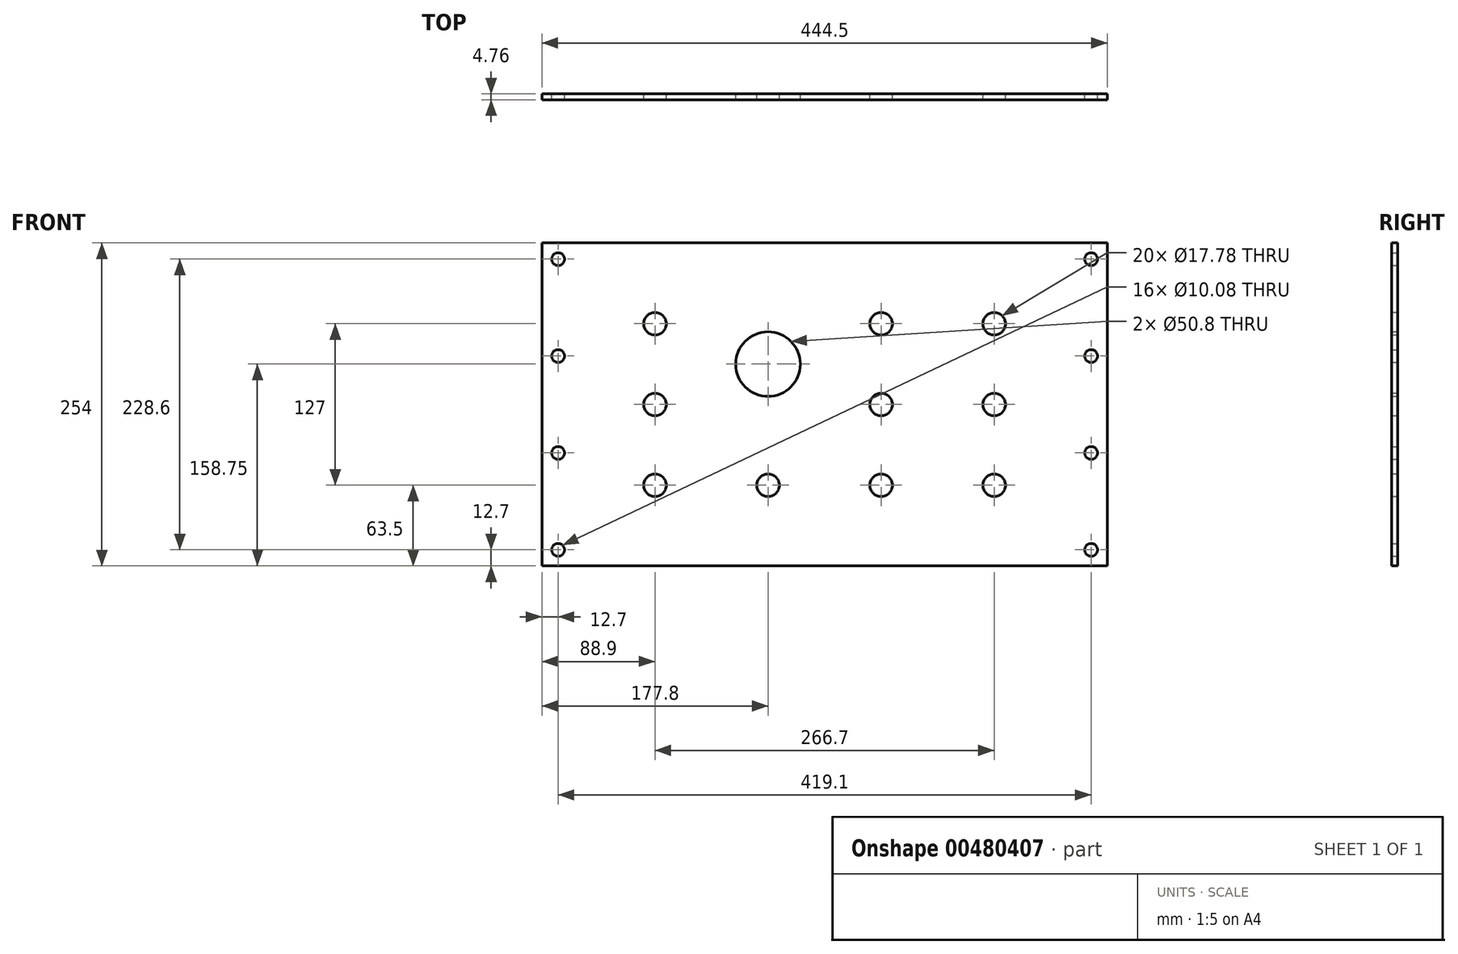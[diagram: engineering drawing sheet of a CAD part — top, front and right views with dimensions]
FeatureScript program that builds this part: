
annotation { "Feature Type Name" : "Feature", "Feature Type Description" : "" }
export const myFeature = defineFeature(function(context is Context, id is Id, definition is map)
    precondition{}
    {
        {
            var Q0;
            Q0=qCreatedBy(makeId("Front.planeOp"),FACE);
            var sketch = newSketch(context, id + "F0", { "sketchPlane" : qUnion([Q0])});
            skLineSegment(sketch, "E0.bottom", {"start": v(-222.25, 127) * mm, "end": v(222.25, 127) * mm});
            skLineSegment(sketch, "E0.top", {"start": v(-222.25, -127) * mm, "end": v(222.25, -127) * mm});
            skLineSegment(sketch, "E0.left", {"start": v(-222.25, 127) * mm, "end": v(-222.25, -127) * mm});
            skLineSegment(sketch, "E0.right", {"start": v(222.25, 127) * mm, "end": v(222.25, -127) * mm});
            skPoint(sketch, "E0.middle", {"position": v(0, 0) * mm});
            skCircle(sketch, "E1", {"center": v(-44.45, 31.75) * mm, "radius": 25.4 * mm});
            skCircle(sketch, "E2", {"center": v(209.55, 114.3) * mm, "radius": 5.04 * mm});
            skCircle(sketch, "E3", {"center": v(209.55, 38.1) * mm, "radius": 5.04 * mm});
            skCircle(sketch, "E4", {"center": v(209.55, -38.1) * mm, "radius": 5.04 * mm});
            skCircle(sketch, "E5", {"center": v(209.55, -114.3) * mm, "radius": 5.04 * mm});
            skCircle(sketch, "E6", {"center": v(-209.55, 114.3) * mm, "radius": 5.04 * mm});
            skCircle(sketch, "E7", {"center": v(-209.55, 38.1) * mm, "radius": 5.04 * mm});
            skCircle(sketch, "E8", {"center": v(-209.55, -38.1) * mm, "radius": 5.04 * mm});
            skCircle(sketch, "E9", {"center": v(-209.55, -114.3) * mm, "radius": 5.04 * mm});
            skCircle(sketch, "E10", {"center": v(-133.35, 63.5) * mm, "radius": 8.9 * mm});
            skCircle(sketch, "E11", {"center": v(-133.35, 0) * mm, "radius": 8.9 * mm});
            skCircle(sketch, "E12", {"center": v(-133.35, -63.5) * mm, "radius": 8.9 * mm});
            skCircle(sketch, "E13", {"center": v(-44.45, -63.5) * mm, "radius": 8.9 * mm});
            skCircle(sketch, "E14", {"center": v(44.45, -63.5) * mm, "radius": 8.9 * mm});
            skCircle(sketch, "E15", {"center": v(133.35, -63.5) * mm, "radius": 8.9 * mm});
            skCircle(sketch, "E16", {"center": v(133.35, 0) * mm, "radius": 8.9 * mm});
            skCircle(sketch, "E17", {"center": v(44.45, 0) * mm, "radius": 8.9 * mm});
            skCircle(sketch, "E18", {"center": v(44.45, 63.5) * mm, "radius": 8.9 * mm});
            skCircle(sketch, "E19", {"center": v(133.35, 63.5) * mm, "radius": 8.9 * mm});
            skSolve(sketch);
        }
        {
            var Q0;
            Q0=qSketchRegion(id+"F0",true);
            extrude(context, id + "F1", {"entities" : qUnion([Q0]), "depth" : 4.76 * mm});
        }
        {
            var Q0;
            Q0 = qSketchRegion(id + "F0", true);
            extrude(context, id + "F2", {"entities" : qUnion([Q0]), "depth" : 4.76 * mm});
        }
    });
